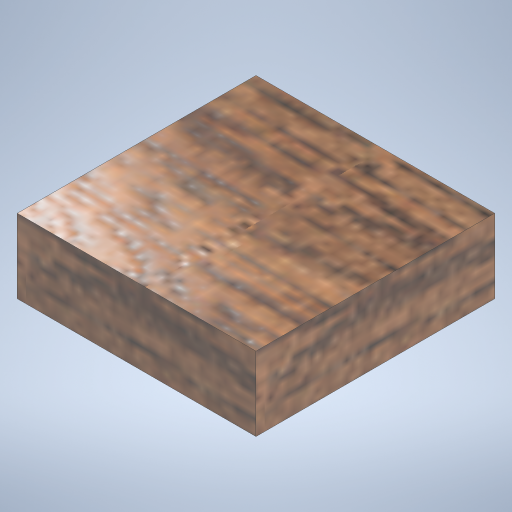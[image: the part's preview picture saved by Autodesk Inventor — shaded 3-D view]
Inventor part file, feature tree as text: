
AUTODESK INVENTOR PART (.ipt)
format: ipt  version: 2023 (Build 270158000, 158)  size: 425,472 bytes
history: native  units: mm
features: other x1, extrude x1, sketch x1
ambient origin geometry x8: Origin, YZ Plane, XZ Plane, XY Plane, X Axis, Y Axis, Z Axis, Center Point
bodies: Body1 (feature_tree)
feature tree (3):
  other  "솔리드1"
  extrude  "돌출1"  Depth=100.0mm
  sketch  "스케치1"
